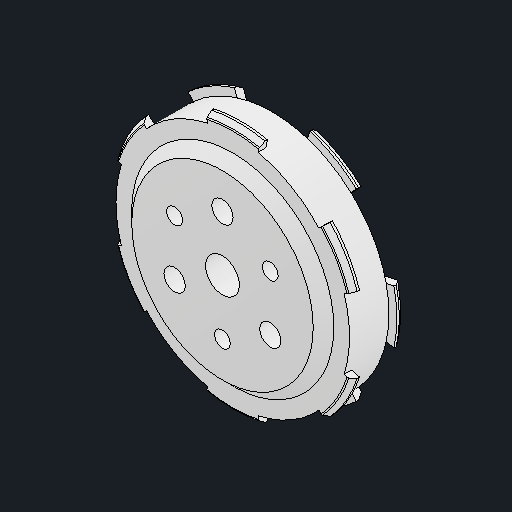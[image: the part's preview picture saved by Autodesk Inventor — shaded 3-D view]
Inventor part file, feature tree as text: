
AUTODESK INVENTOR PART (.ipt)
format: ipt  version: 2023.2 (Build 272271030, 271C)  size: 430,592 bytes
history: native  units: mm
features: sketch x15, extrude x13, chamfer x3, pattern_circular x3, projected_geometry x3, other x2, fillet x2, plane x1, revolve x1
ambient origin geometry x8: Origin, YZ Plane, XZ Plane, XY Plane, X Axis, Y Axis, Z Axis, Center Point
bodies: Body1 (feature_tree)
feature tree (43):
  other  "ソリッド1"
  extrude  "押し出し1"  Depth=0.5mm TaperAngle=0.0deg
  extrude  "押し出し2"  Depth=0.5mm
  sketch  "スケッチ3"
  plane  "Work Plane2"
  revolve  "回転2"
  chamfer  "面取り1"  Distance=1.3mm
  chamfer  "面取り2"  Distance=26.0mm
  extrude  "押し出し4"  Depth=1.0mm
  extrude  "押し出し5"  Depth=1.0mm
  pattern_circular  "Circular Pattern6"  [2 undecoded]
  extrude  "押し出し6"  TaperAngle=90.0deg  [1 undecoded]
  extrude  "押し出し7"  Depth=0.5mm TaperAngle=45.0deg
  extrude  "押し出し9"  Depth=0.5mm TaperAngle=45.0deg
  extrude  "押し出し10"  Depth=0.5mm
  extrude  "押し出し11"  Depth=0.5mm
  extrude  "押し出し12"  TaperAngle=150.0deg  [1 undecoded]
  extrude  "押し出し13"  Depth=1.3mm TaperAngle=0.0deg
  pattern_circular  "円形状パターン5"  [2 undecoded]
  sketch  "スケッチ18"
  other  "作業平面1"
  extrude  "押し出し14"  Depth=0.5mm
  fillet  "フィレット1"  Radius=1.3mm
  fillet  "フィレット3"  Radius=4.5mm
  chamfer  "Chamfer3"  Distance=1.3mm
  extrude  "Extrusion15"  Depth=7.0mm
  pattern_circular  "Circular Pattern7"  [2 undecoded]
  sketch  "スケッチ1"
  sketch  "スケッチ2"
  sketch  "スケッチ6"
  sketch  "スケッチ7"
  sketch  "スケッチ8"
  sketch  "スケッチ10"
  sketch  "スケッチ13"
  sketch  "スケッチ14"
  sketch  "スケッチ15"
  sketch  "スケッチ16"
  sketch  "スケッチ17"
  sketch  "スケッチ19"
  projected_geometry  "Projected Loop3"
  projected_geometry  "Projected Loop4"
  sketch  "Sketch20"  dims[d0=31.6mm d1=7.3mm d2=0.0mm d3=3.0mm d4=1.3mm d5=0.0mm d6=26.0mm d18=1.0mm d19=1.0mm d20=1.0mm d21=90.0deg d22=0.7mm d23=0.5mm d24=45.0deg d25=0.7mm d26=0.5mm d27=45.0deg d28=5.0mm d29=5.0mm d30=150.0deg d31=1.3mm d32=0.0mm d36=5.0mm d37=5.0mm d38=1.3mm d39=0.0mm d43=4.5mm d44=0.0mm d45=1.3mm d46=0.0mm d53=7.0mm d54=5.0mm d55=7.0mm d56=30.0mm d58=360.0deg d60=5.8mm d61=0.0mm d62=7.0mm d63=7.0mm d64=0.0mm d65=2.7mm d66=0.0mm d67=0.0mm d71=4.3mm d72=0.0mm d73=0.0mm d74=7.0mm d75=2.0mm d76=0.0mm d77=0.0mm d78=30.0mm d79=360.0deg d81=1.0mm d82=1.0mm d83=3.0mm d84=7.0mm d85=0.0mm d86=0.2mm d88=0.2mm d93=25.6mm d94=30.0deg d95=60.0mm d96=360.0deg d98=1.3mm d99=2.0mm d100=45.0deg d101=1.3mm d102=0.5mm d103=0.0mm d104=30.0mm d105=360.0deg d33=0.5mm d34=0.872665mm d107=0.5mm d108=0.872665mm d109=0.5mm d110=0.872665mm]
  projected_geometry  "Projected Loop5"
note: 8 required parameter values undecoded (feature->parameter linkage not recoverable at this tier; creation-order binding heuristic only, values carry confidence <= 0.55)
